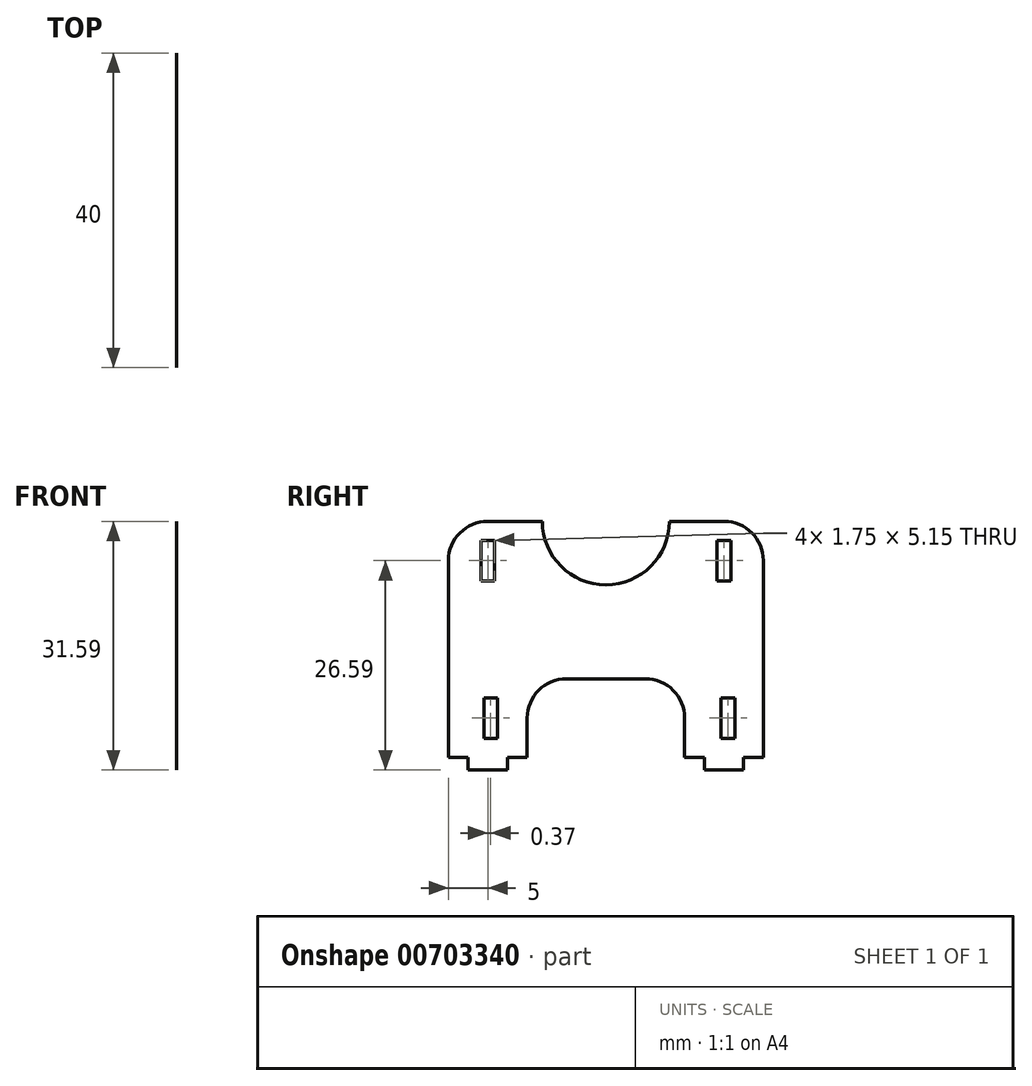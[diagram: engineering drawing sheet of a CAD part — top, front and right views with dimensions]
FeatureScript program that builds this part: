
annotation { "Feature Type Name" : "Feature", "Feature Type Description" : "" }
export const myFeature = defineFeature(function(context is Context, id is Id, definition is map)
    precondition{}
    {
        {
            var Q0;
            Q0=qCreatedBy(makeId("Right.planeOp"),FACE);
            var sketch = newSketch(context, id + "F0", { "sketchPlane" : qUnion([Q0])});
            skLineSegment(sketch, "E0.bottom", {"start": v(20, 15) * mm, "end": v(-20, 15) * mm});
            skLineSegment(sketch, "E0.top", {"start": v(20, -15) * mm, "end": v(-20, -15) * mm});
            skLineSegment(sketch, "E0.left", {"start": v(20, 15) * mm, "end": v(20, -15) * mm});
            skLineSegment(sketch, "E0.right", {"start": v(-20, 15) * mm, "end": v(-20, -15) * mm});
            skPoint(sketch, "E0.middle", {"position": v(0, 0) * mm});
            skCircle(sketch, "E1", {"center": v(0, 15) * mm, "radius": 8.07 * mm});
            skLineSegment(sketch, "E2", {"start": v(-17.5, -15) * mm, "end": v(-17.5, -16.59) * mm});
            skLineSegment(sketch, "E3", {"start": v(-17.5, -16.59) * mm, "end": v(-12.5, -16.59) * mm});
            skLineSegment(sketch, "E4", {"start": v(-12.5, -16.59) * mm, "end": v(-12.5, -15) * mm});
            skLineSegment(sketch, "E5", {"start": v(17.5, -15) * mm, "end": v(17.5, -16.59) * mm});
            skLineSegment(sketch, "E6", {"start": v(17.5, -16.59) * mm, "end": v(12.5, -16.59) * mm});
            skLineSegment(sketch, "E7", {"start": v(12.5, -16.59) * mm, "end": v(12.5, -15) * mm});
            skLineSegment(sketch, "E8.bottom", {"start": v(-14.13, 12.57) * mm, "end": v(-15.87, 12.57) * mm});
            skLineSegment(sketch, "E8.top", {"start": v(-14.13, 7.42) * mm, "end": v(-15.87, 7.42) * mm});
            skLineSegment(sketch, "E8.left", {"start": v(-14.13, 12.57) * mm, "end": v(-14.13, 7.42) * mm});
            skLineSegment(sketch, "E8.right", {"start": v(-15.87, 12.57) * mm, "end": v(-15.87, 7.42) * mm});
            skPoint(sketch, "E8.middle", {"position": v(-15, 10) * mm});
            skLineSegment(sketch, "E9.bottom", {"start": v(15.87, 12.57) * mm, "end": v(14.13, 12.57) * mm});
            skLineSegment(sketch, "E9.top", {"start": v(15.87, 7.42) * mm, "end": v(14.13, 7.42) * mm});
            skLineSegment(sketch, "E9.left", {"start": v(15.87, 12.57) * mm, "end": v(15.87, 7.42) * mm});
            skLineSegment(sketch, "E9.right", {"start": v(14.13, 12.57) * mm, "end": v(14.13, 7.42) * mm});
            skPoint(sketch, "E9.middle", {"position": v(15, 10) * mm});
            skLineSegment(sketch, "E10.bottom", {"start": v(16.38, -7.43) * mm, "end": v(14.63, -7.43) * mm});
            skLineSegment(sketch, "E10.top", {"start": v(16.38, -12.58) * mm, "end": v(14.63, -12.58) * mm});
            skLineSegment(sketch, "E10.left", {"start": v(16.38, -7.43) * mm, "end": v(16.38, -12.58) * mm});
            skLineSegment(sketch, "E10.right", {"start": v(14.63, -7.43) * mm, "end": v(14.63, -12.58) * mm});
            skPoint(sketch, "E10.middle", {"position": v(15.5, -10) * mm});
            skLineSegment(sketch, "E11.bottom", {"start": v(-13.76, -7.42) * mm, "end": v(-15.5, -7.42) * mm});
            skLineSegment(sketch, "E11.top", {"start": v(-13.76, -12.57) * mm, "end": v(-15.5, -12.57) * mm});
            skLineSegment(sketch, "E11.left", {"start": v(-13.76, -7.42) * mm, "end": v(-13.76, -12.57) * mm});
            skLineSegment(sketch, "E11.right", {"start": v(-15.5, -7.42) * mm, "end": v(-15.5, -12.57) * mm});
            skPoint(sketch, "E11.middle", {"position": v(-14.63, -10) * mm});
            skLineSegment(sketch, "E12", {"start": v(-10, -15) * mm, "end": v(-10, -5) * mm});
            skLineSegment(sketch, "E13", {"start": v(-10, -5) * mm, "end": v(10, -5) * mm});
            skLineSegment(sketch, "E14", {"start": v(10, -5) * mm, "end": v(10, -15) * mm});
            skSolve(sketch);
        }
        {
            var Q0;
            {var subQ3=sQuery(id+"F0.wireOp",EDGE,"E0.left");Q0=makeQuery(id+"F0.imprint","IMPRINT",FACE,{"disambiguationData":[TD([[makeQuery(id+"F0.imprint","IMPRINT",EDGE,{"derivedFrom":subQ3}),-1.0]])]});}
            var Q1;
            {var subQ0=sQuery(id+"F0.wireOp",EDGE,"E2");Q1=makeQuery(id+"F0.imprint","IMPRINT",FACE,{"disambiguationData":[TD([[makeQuery(id+"F0.imprint","IMPRINT",EDGE,{"derivedFrom":subQ0}),1.0]])]});}
            var Q2;
            {var subQ0=sQuery(id+"F0.wireOp",EDGE,"E5");Q2=makeQuery(id+"F0.imprint","IMPRINT",FACE,{"disambiguationData":[TD([[makeQuery(id+"F0.imprint","IMPRINT",EDGE,{"derivedFrom":subQ0}),-1.0]])]});}
            extrude(context, id + "F1", {"entities" : qUnion([Q0, Q1, Q2]), "depth" : 1 / 406.4 * mm, "offsetDistance" : 25 * mm});
        }
        {
            var Q0;
            Q0=makeQuery(id+"F1.opExtrude","SWEPT_EDGE",EDGE,{"disambiguationData":[OSD([sQuery(id+"F0.wireOp",EDGE,"E12"),sQuery(id+"F0.wireOp",EDGE,"E13")])]});
            var Q1;
            Q1=makeQuery(id+"F1.opExtrude","SWEPT_EDGE",EDGE,{"disambiguationData":[OSD([sQuery(id+"F0.wireOp",EDGE,"E13"),sQuery(id+"F0.wireOp",EDGE,"E14")])]});
            var Q2;
            Q2=makeQuery(id+"F1.opExtrude","SWEPT_EDGE",EDGE,{"disambiguationData":[OSD([sQuery(id+"F0.wireOp",EDGE,"E0.bottom"),sQuery(id+"F0.wireOp",EDGE,"E0.left")])]});
            var Q3;
            Q3=makeQuery(id+"F1.opExtrude","SWEPT_EDGE",EDGE,{"disambiguationData":[OSD([sQuery(id+"F0.wireOp",EDGE,"E0.bottom"),sQuery(id+"F0.wireOp",EDGE,"E0.right")])]});
            fillet(context, id + "F2", {"entities" : qUnion([Q0, Q1, Q2, Q3]), "radius" : 5 * mm, "tangentPropagation" : true, "allowEdgeOverflow" : false});
        }
    });
